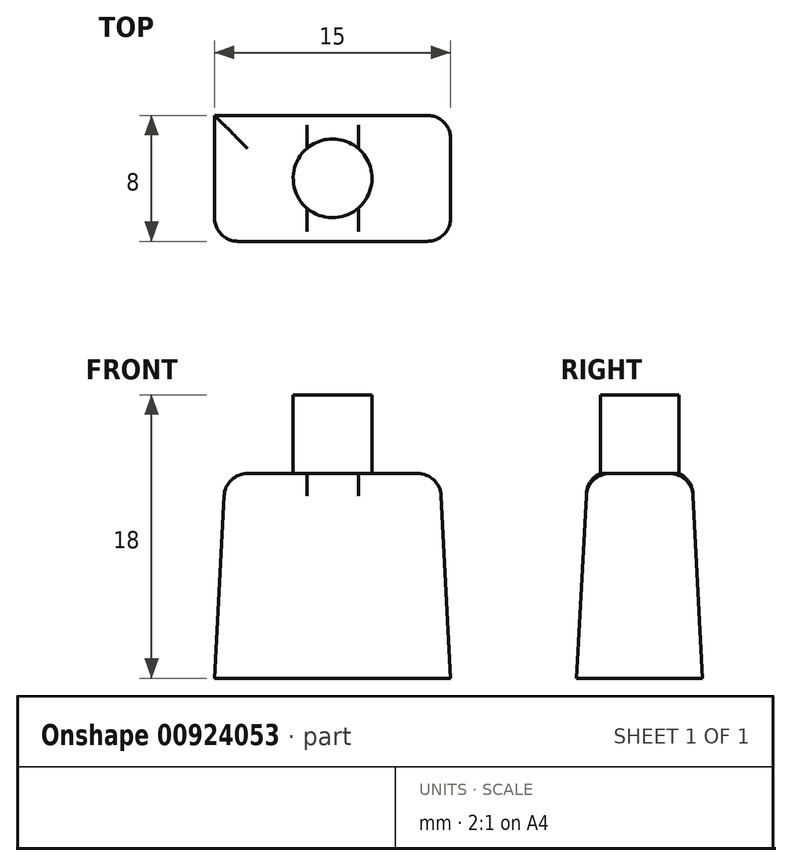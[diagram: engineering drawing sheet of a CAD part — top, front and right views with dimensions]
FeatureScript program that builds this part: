
annotation { "Feature Type Name" : "Feature", "Feature Type Description" : "" }
export const myFeature = defineFeature(function(context is Context, id is Id, definition is map)
    precondition{}
    {
        {
            var Q0;
            Q0=qCreatedBy(makeId("Top.planeOp"),FACE);
            var sketch = newSketch(context, id + "F0", { "sketchPlane" : qUnion([Q0])});
            skLineSegment(sketch, "E0.bottom", {"start": v(7.5, 4) * mm, "end": v(-7.5, 4) * mm});
            skLineSegment(sketch, "E0.top", {"start": v(7.5, -4) * mm, "end": v(-7.5, -4) * mm});
            skLineSegment(sketch, "E0.left", {"start": v(7.5, 4) * mm, "end": v(7.5, -4) * mm});
            skLineSegment(sketch, "E0.right", {"start": v(-7.5, 4) * mm, "end": v(-7.5, -4) * mm});
            skPoint(sketch, "E0.middle", {"position": v(0, 0) * mm});
            skSolve(sketch);
        }
        {
            var Q0;
            Q0 = qSketchRegion(id + "F0", true);
            extrude(context, id + "F1", {"entities" : qUnion([Q0]), "depth" : 13 * mm, "offsetDistance" : 25 * mm, "hasDraft" : true, "draftAngle" : 3 * degree, "draftPullDirection" : true});
        }
        {
            var Q0;
            Q0=makeQuery(id+"F1.opExtrude","CAP_FACE",FACE,{"disambiguationData":[OSD([sQuery(id+"F0.wireOp",EDGE,"E0.bottom"),sQuery(id+"F0.wireOp",EDGE,"E0.top"),sQuery(id+"F0.wireOp",EDGE,"E0.left"),sQuery(id+"F0.wireOp",EDGE,"E0.right")])],"isStart":false});
            var sketch = newSketch(context, id + "F2", { "sketchPlane" : qUnion([Q0])});
            skCircle(sketch, "E1", {"center": v(0, 0) * mm, "radius": 2.5 * mm});
            skSolve(sketch);
        }
        {
            var Q0;
            Q0=makeQuery(id+"F2.imprint","IMPRINT",FACE,{"disambiguationData":[TD([[makeQuery(id+"F2.imprint","IMPRINT",EDGE,{"derivedFrom":sQuery(id+"F2.wireOp",EDGE,"E1")}),1.0]])]});
            extrude(context, id + "F3", {"entities" : qUnion([Q0]), "operationType" : NewBodyOperationType.ADD, "depth" : 5 * mm, "offsetDistance" : 25 * mm});
        }
        {
            var Q0;
            Q0=makeQuery(id+"F1.opExtrude","CAP_EDGE",EDGE,{"disambiguationData":[OSD([sQuery(id+"F0.wireOp",EDGE,"E0.right")])],"isStart":false});
            var Q1;
            Q1=makeQuery(id+"F1.opExtrude","SWEPT_EDGE",EDGE,{"disambiguationData":[OSD([sQuery(id+"F0.wireOp",EDGE,"E0.top"),sQuery(id+"F0.wireOp",EDGE,"E0.right")])]});
            var Q2;
            Q2=makeQuery(id+"F1.opExtrude","SWEPT_EDGE",EDGE,{"disambiguationData":[OSD([sQuery(id+"F0.wireOp",EDGE,"E0.top"),sQuery(id+"F0.wireOp",EDGE,"E0.left")])]});
            var Q3;
            Q3=makeQuery(id+"F1.opExtrude","SWEPT_EDGE",EDGE,{"disambiguationData":[OSD([sQuery(id+"F0.wireOp",EDGE,"E0.bottom"),sQuery(id+"F0.wireOp",EDGE,"E0.left")])]});
            var Q4;
            Q4=makeQuery(id+"F1.opExtrude","CAP_EDGE",EDGE,{"disambiguationData":[OSD([sQuery(id+"F0.wireOp",EDGE,"E0.bottom")])],"isStart":false});
            var Q5;
            Q5=makeQuery(id+"F1.opExtrude","CAP_EDGE",EDGE,{"disambiguationData":[OSD([sQuery(id+"F0.wireOp",EDGE,"E0.left")])],"isStart":false});
            var Q6;
            Q6=makeQuery(id+"F1.opExtrude","CAP_EDGE",EDGE,{"disambiguationData":[OSD([sQuery(id+"F0.wireOp",EDGE,"E0.top")])],"isStart":false});
            fillet(context, id + "F4", {"entities" : qUnion([Q0, Q1, Q2, Q3, Q4, Q5, Q6]), "radius" : 1.5 * mm, "tangentPropagation" : true, "allowEdgeOverflow" : false});
        }
    });
